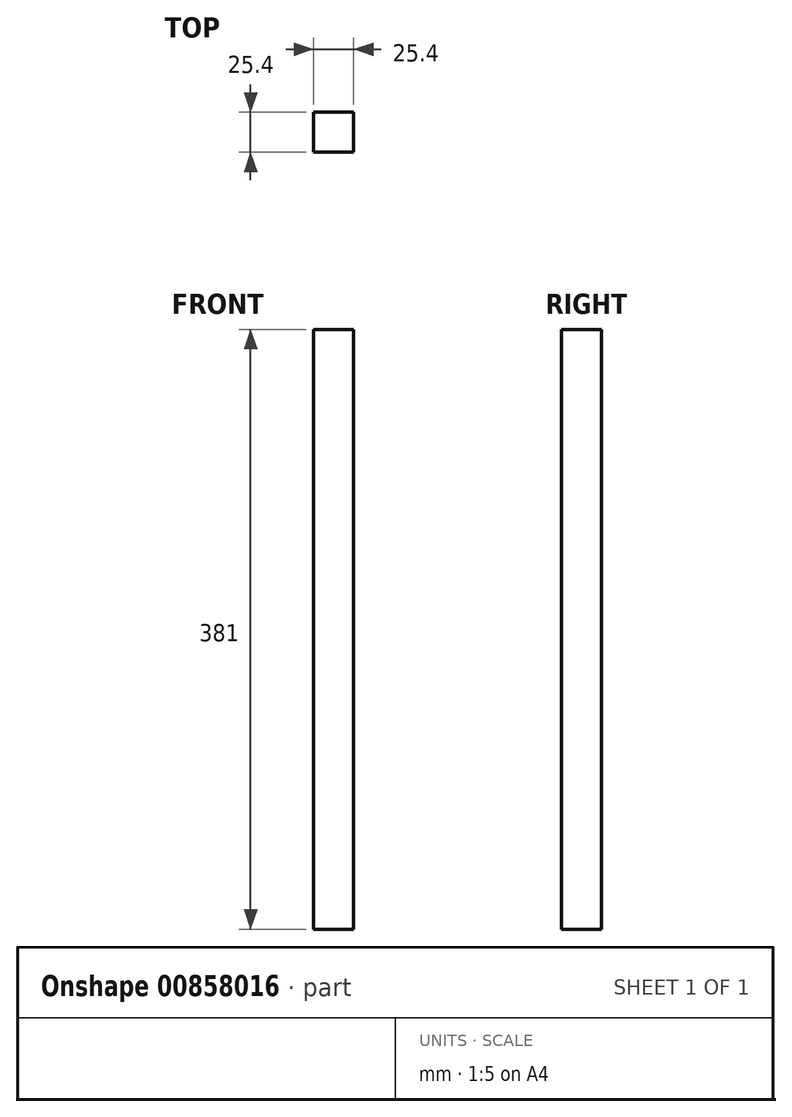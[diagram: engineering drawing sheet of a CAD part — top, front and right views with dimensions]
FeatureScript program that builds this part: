
annotation { "Feature Type Name" : "Feature", "Feature Type Description" : "" }
export const myFeature = defineFeature(function(context is Context, id is Id, definition is map)
    precondition{}
    {
        {
            var Q0;
            Q0=qCreatedBy(makeId("Front.planeOp"),FACE);
            var sketch = newSketch(context, id + "F0", { "sketchPlane" : qUnion([Q0])});
            skLineSegment(sketch, "E0.bottom", {"start": v(0, 0) * mm, "end": v(25.4, 0) * mm});
            skLineSegment(sketch, "E0.top", {"start": v(0, 381) * mm, "end": v(25.4, 381) * mm});
            skLineSegment(sketch, "E0.left", {"start": v(0, 0) * mm, "end": v(0, 381) * mm});
            skLineSegment(sketch, "E0.right", {"start": v(25.4, 0) * mm, "end": v(25.4, 381) * mm});
            skSolve(sketch);
        }
        {
            var Q0;
            Q0 = qSketchRegion(id + "F0", true);
            extrude(context, id + "F1", {"entities" : qUnion([Q0]), "depth" : 25.4 * mm, "offsetDistance" : 25.4 * mm});
        }
    });
